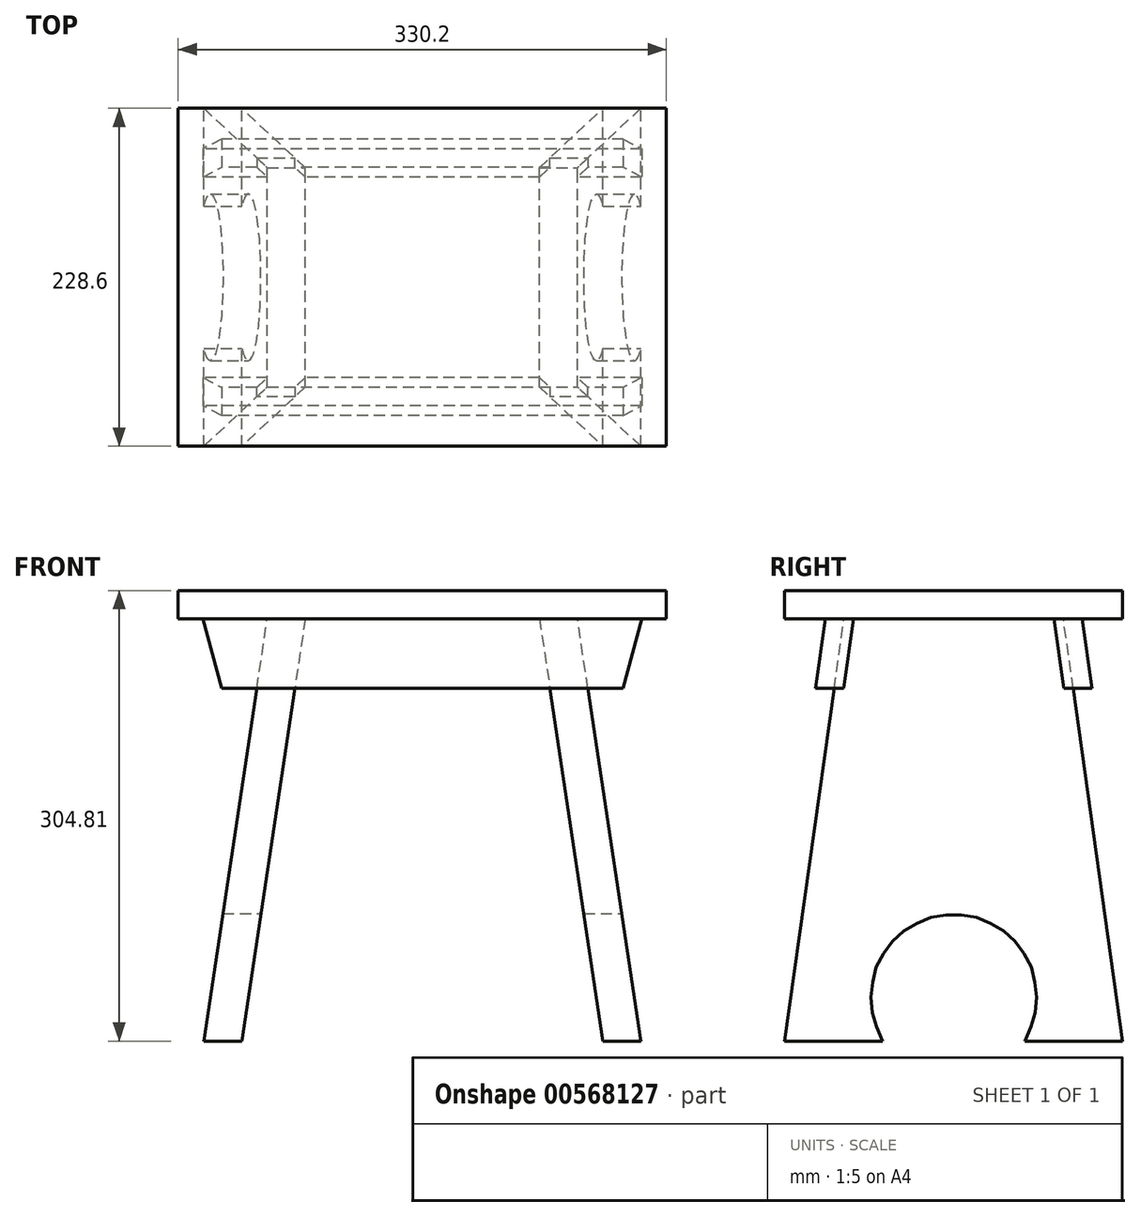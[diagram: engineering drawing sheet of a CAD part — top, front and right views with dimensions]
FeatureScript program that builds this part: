
annotation { "Feature Type Name" : "Feature", "Feature Type Description" : "" }
export const myFeature = defineFeature(function(context is Context, id is Id, definition is map)
    precondition{}
    {
        {
            var Q0;
            Q0=qCreatedBy(makeId("Front.planeOp"),FACE);
            var sketch = newSketch(context, id + "F0", { "sketchPlane" : qUnion([Q0])});
            skLineSegment(sketch, "E0.bottom", {"start": v(-165.1, 9.53) * mm, "end": v(165.1, 9.53) * mm});
            skLineSegment(sketch, "E0.top", {"start": v(-165.1, -9.52) * mm, "end": v(165.1, -9.52) * mm});
            skLineSegment(sketch, "E0.left", {"start": v(-165.1, 9.53) * mm, "end": v(-165.1, -9.52) * mm});
            skLineSegment(sketch, "E0.right", {"start": v(165.1, 9.53) * mm, "end": v(165.1, -9.52) * mm});
            skPoint(sketch, "E0.middle", {"position": v(0, 0) * mm});
            skLineSegment(sketch, "E1.bottom", {"start": v(-165.1, -9.52) * mm, "end": v(165.1, -9.52) * mm, "construction": true});
            skLineSegment(sketch, "E1.top", {"start": v(-165.1, -295.28) * mm, "end": v(165.1, -295.28) * mm, "construction": true});
            skLineSegment(sketch, "E1.left", {"start": v(-165.1, -9.52) * mm, "end": v(-165.1, -295.28) * mm, "construction": true});
            skLineSegment(sketch, "E1.right", {"start": v(165.1, -9.52) * mm, "end": v(165.1, -295.27) * mm, "construction": true});
            skLineSegment(sketch, "E2", {"start": v(104.9, -9.52) * mm, "end": v(147.77, -295.28) * mm});
            skLineSegment(sketch, "E3", {"start": v(147.77, -295.27) * mm, "end": v(122.1, -295.27) * mm});
            skLineSegment(sketch, "E4", {"start": v(122.1, -295.27) * mm, "end": v(79.2, -9.52) * mm});
            skLineSegment(sketch, "E5", {"start": v(79.2, -9.52) * mm, "end": v(104.9, -9.52) * mm});
            skLineSegment(sketch, "E6", {"start": v(0, 0) * mm, "end": v(0, -295.28) * mm, "construction": true});
            skLineSegment(sketch, "E7.MirrorCS", {"start": v(-104.9, -9.52) * mm, "end": v(-147.77, -295.28) * mm});
            skLineSegment(sketch, "E8.MirrorCS", {"start": v(-79.2, -9.52) * mm, "end": v(-104.9, -9.52) * mm});
            skLineSegment(sketch, "E9.MirrorCS", {"start": v(-147.77, -295.28) * mm, "end": v(-122.1, -295.28) * mm});
            skLineSegment(sketch, "E10.MirrorCS", {"start": v(-122.1, -295.28) * mm, "end": v(-79.2, -9.52) * mm});
            skLineSegment(sketch, "E11.top", {"start": v(-165.1, -56.79) * mm, "end": v(165.1, -56.79) * mm});
            skLineSegment(sketch, "E11.left", {"start": v(-165.1, -9.52) * mm, "end": v(-165.1, -56.79) * mm});
            skLineSegment(sketch, "E11.right", {"start": v(165.1, -9.52) * mm, "end": v(165.1, -56.79) * mm});
            skLineSegment(sketch, "E12", {"start": v(148.48, -9.52) * mm, "end": v(135.79, -56.79) * mm});
            skLineSegment(sketch, "E13.MirrorCS", {"start": v(-148.48, -9.52) * mm, "end": v(-135.79, -56.79) * mm});
            skSolve(sketch);
        }
        {
            var Q0;
            Q0=qCreatedBy(makeId("Front.planeOp"),FACE);
            var sketch = newSketch(context, id + "F1", { "sketchPlane" : qUnion([Q0])});
            skSolve(sketch);
        }
        {
            var Q0;
            Q0 = qSketchRegion(id + "F1", true);
            var Q1;
            Q1=makeQuery(id+"F0.imprint","IMPRINT",FACE,{"disambiguationData":[TD([[makeQuery(id+"F0.imprint","IMPRINT",EDGE,{"derivedFrom":sQuery(id+"F0.wireOp",EDGE,"E0.bottom")}),-1.0]])]});
            extrude(context, id + "F2", {"entities" : qUnion([Q0, Q1]), "endBound" : BoundingType.SYMMETRIC, "depth" : 228.6 * mm, "offsetDistance" : 25.4 * mm});
        }
        {
            var Q0;
            {var subQ0=sQuery(id+"F0.wireOp",EDGE,"E9.MirrorCS");Q0=makeQuery(id+"F0.imprint","IMPRINT",FACE,{"disambiguationData":[TD([[makeQuery(id+"F0.imprint","IMPRINT",EDGE,{"derivedFrom":subQ0}),1.0]])]});}
            var Q1;
            {var subQ0=sQuery(id+"F0.wireOp",EDGE,"E0.top");var subQ1=sQuery(id+"F0.wireOp",EDGE,"E7.MirrorCS");var subQ2=makeQuery(id+"F0.imprint","INTERSECT",VERTEX,{"derivedFrom":[subQ1,subQ0]});Q1=makeQuery(id+"F0.imprint","IMPRINT",FACE,{"disambiguationData":[TD([[makeQuery(id+"F0.imprint","IMPRINT",EDGE,{"disambiguationData":[TD([[subQ2,-1.0]])],"derivedFrom":subQ1}),1.0]])]});}
            var Q2;
            {var subQ0=sQuery(id+"F0.wireOp",EDGE,"E0.top");var subQ1=sQuery(id+"F0.wireOp",EDGE,"E2");var subQ2=makeQuery(id+"F0.imprint","INTERSECT",VERTEX,{"derivedFrom":[subQ1,subQ0]});Q2=makeQuery(id+"F0.imprint","IMPRINT",FACE,{"disambiguationData":[TD([[makeQuery(id+"F0.imprint","IMPRINT",EDGE,{"disambiguationData":[TD([[subQ2,-1.0]])],"derivedFrom":subQ1}),-1.0]])]});}
            var Q3;
            {var subQ0=sQuery(id+"F0.wireOp",EDGE,"E3");Q3=makeQuery(id+"F0.imprint","IMPRINT",FACE,{"disambiguationData":[TD([[makeQuery(id+"F0.imprint","IMPRINT",EDGE,{"derivedFrom":subQ0}),-1.0]])]});}
            var Q4;
            Q4=makeQuery(id+"F2.opExtrude","CAP_VERTEX",VERTEX,{"disambiguationData":[OSD([sQuery(id+"F0.wireOp",EDGE,"E0.right"),sQuery(id+"F0.wireOp",EDGE,"E0.top"),sQuery(id+"F0.wireOp",EDGE,"E11.right")])],"isStart":false});
            var Q5;
            Q5=makeQuery(id+"F2.opExtrude","CAP_VERTEX",VERTEX,{"disambiguationData":[OSD([sQuery(id+"F0.wireOp",EDGE,"E0.right"),sQuery(id+"F0.wireOp",EDGE,"E0.top"),sQuery(id+"F0.wireOp",EDGE,"E11.right")])],"isStart":true});
            extrude(context, id + "F3", {"entities" : qUnion([Q0, Q1, Q2, Q3]), "endBound" : BoundingType.UP_TO_VERTEX, "depth" : 25.4 * mm, "endBoundEntityVertex" : qUnion([Q4]), "offsetDistance" : 25.4 * mm, "hasSecondDirection" : true, "secondDirectionBound" : SecondDirectionBoundingType.UP_TO_VERTEX, "secondDirectionOppositeDirection" : true, "secondDirectionDepth" : 25.4 * mm, "secondDirectionBoundEntityVertex" : qUnion([Q5])});
        }
        {
            var Q0;
            Q0=qCreatedBy(makeId("Right.planeOp"),FACE);
            var sketch = newSketch(context, id + "F4", { "sketchPlane" : qUnion([Q0])});
            skLineSegment(sketch, "E14.0.0", {"start": v(114.3, -9.52) * mm, "end": v(-114.3, -9.52) * mm});
            skLineSegment(sketch, "E14.0.1", {"start": v(-114.3, -9.52) * mm, "end": v(-114.3, -295.28) * mm});
            skLineSegment(sketch, "E14.0.2", {"start": v(-114.3, -295.28) * mm, "end": v(114.3, -295.28) * mm});
            skLineSegment(sketch, "E14.0.3", {"start": v(114.3, -295.28) * mm, "end": v(114.3, -9.52) * mm});
            skLineSegment(sketch, "E15", {"start": v(-114.3, -295.27) * mm, "end": v(-74.14, -9.52) * mm});
            skLineSegment(sketch, "E16.MirrorCS", {"start": v(114.3, -295.27) * mm, "end": v(74.14, -9.52) * mm});
            skArc(sketch, "E17", {"start": v(48.03, -295.28) * mm, "mid": v(0, -209.18) * mm, "end": v(-48.03, -295.28) * mm});
            skLineSegment(sketch, "E18", {"start": v(0, -265.62) * mm, "end": v(0, -265.62) * mm});
            skSolve(sketch);
        }
        {
            var Q0;
            {var subQ0=sQuery(id+"F4.wireOp",EDGE,"E14.0.1");Q0=makeQuery(id+"F4.imprint","IMPRINT",FACE,{"disambiguationData":[TD([[makeQuery(id+"F4.imprint","IMPRINT",EDGE,{"derivedFrom":subQ0}),1.0]])]});}
            var Q1;
            {var subQ0=sQuery(id+"F4.wireOp",EDGE,"E17");Q1=makeQuery(id+"F4.imprint","IMPRINT",FACE,{"disambiguationData":[TD([[makeQuery(id+"F4.imprint","IMPRINT",EDGE,{"derivedFrom":subQ0}),1.0]])]});}
            var Q2;
            {var subQ0=sQuery(id+"F4.wireOp",EDGE,"E14.0.3");Q2=makeQuery(id+"F4.imprint","IMPRINT",FACE,{"disambiguationData":[TD([[makeQuery(id+"F4.imprint","IMPRINT",EDGE,{"derivedFrom":subQ0}),1.0]])]});}
            extrude(context, id + "F5", {"entities" : qUnion([Q0, Q1, Q2]), "operationType" : NewBodyOperationType.REMOVE, "endBound" : BoundingType.THROUGH_ALL, "oppositeDirection" : true, "depth" : 25.4 * mm, "offsetDistance" : 25.4 * mm, "hasSecondDirection" : true, "secondDirectionBound" : SecondDirectionBoundingType.THROUGH_ALL, "secondDirectionOppositeDirection" : false, "secondDirectionDepth" : 25.4 * mm});
        }
        {
            var Q0;
            Q0=qCreatedBy(makeId("Right.planeOp"),FACE);
            var sketch = newSketch(context, id + "F6", { "sketchPlane" : qUnion([Q0])});
            skLineSegment(sketch, "E19.0", {"start": v(-74.14, -9.52) * mm, "end": v(-114.3, -295.28) * mm});
            skLineSegment(sketch, "E20.0", {"start": v(-114.3, -9.52) * mm, "end": v(114.3, -9.52) * mm});
            skLineSegment(sketch, "E21.0", {"start": v(74.14, -9.53) * mm, "end": v(114.3, -295.28) * mm});
            skLineSegment(sketch, "E22", {"start": v(-86.97, -9.52) * mm, "end": v(-93.6, -56.79) * mm});
            skLineSegment(sketch, "E23", {"start": v(-93.6, -56.79) * mm, "end": v(-74.37, -56.79) * mm});
            skLineSegment(sketch, "E24", {"start": v(-74.37, -56.79) * mm, "end": v(-67.73, -9.52) * mm});
            skLineSegment(sketch, "E25", {"start": v(-67.73, -9.52) * mm, "end": v(-86.97, -9.52) * mm});
            skLineSegment(sketch, "E26", {"start": v(-74.37, -56.79) * mm, "end": v(14.93, -56.79) * mm, "construction": true});
            skLineSegment(sketch, "E27.MirrorCS", {"start": v(74.37, -56.79) * mm, "end": v(67.73, -9.52) * mm});
            skLineSegment(sketch, "E28.MirrorCS", {"start": v(67.73, -9.52) * mm, "end": v(86.97, -9.52) * mm});
            skLineSegment(sketch, "E29.MirrorCS", {"start": v(93.6, -56.79) * mm, "end": v(74.37, -56.79) * mm});
            skLineSegment(sketch, "E30.MirrorCS", {"start": v(86.97, -9.52) * mm, "end": v(93.6, -56.79) * mm});
            skSolve(sketch);
        }
        {
            var Q0;
            {var subQ5=sQuery(id+"F6.wireOp",EDGE,"E24");Q0=makeQuery(id+"F6.imprint","IMPRINT",FACE,{"disambiguationData":[TD([[makeQuery(id+"F6.imprint","IMPRINT",EDGE,{"derivedFrom":subQ5}),1.0]])]});}
            var Q1;
            {var subQ5=sQuery(id+"F6.wireOp",EDGE,"E22");Q1=makeQuery(id+"F6.imprint","IMPRINT",FACE,{"disambiguationData":[TD([[makeQuery(id+"F6.imprint","IMPRINT",EDGE,{"derivedFrom":subQ5}),1.0]])]});}
            var Q2;
            {var subQ5=sQuery(id+"F6.wireOp",EDGE,"E27.MirrorCS");Q2=makeQuery(id+"F6.imprint","IMPRINT",FACE,{"disambiguationData":[TD([[makeQuery(id+"F6.imprint","IMPRINT",EDGE,{"derivedFrom":subQ5}),-1.0]])]});}
            var Q3;
            {var subQ5=sQuery(id+"F6.wireOp",EDGE,"E30.MirrorCS");Q3=makeQuery(id+"F6.imprint","IMPRINT",FACE,{"disambiguationData":[TD([[makeQuery(id+"F6.imprint","IMPRINT",EDGE,{"derivedFrom":subQ5}),-1.0]])]});}
            var Q4;
            Q4=makeQuery(id+"F2.opExtrude","SWEPT_FACE",FACE,{"disambiguationData":[OSD([sQuery(id+"F0.wireOp",EDGE,"E0.right")])]});
            var Q5;
            Q5=makeQuery(id+"F2.opExtrude","SWEPT_FACE",FACE,{"disambiguationData":[OSD([sQuery(id+"F0.wireOp",EDGE,"E0.left")])]});
            extrude(context, id + "F7", {"entities" : qUnion([Q0, Q1, Q2, Q3]), "endBound" : BoundingType.UP_TO_SURFACE, "depth" : 25.4 * mm, "endBoundEntityFace" : qUnion([Q4]), "offsetDistance" : 25.4 * mm, "hasSecondDirection" : true, "secondDirectionBound" : SecondDirectionBoundingType.UP_TO_SURFACE, "secondDirectionOppositeDirection" : true, "secondDirectionDepth" : 25.4 * mm, "secondDirectionBoundEntityFace" : qUnion([Q5])});
        }
        {
            var Q0;
            {var subQ0=sQuery(id+"F0.wireOp",EDGE,"E11.left");Q0=makeQuery(id+"F0.imprint","IMPRINT",FACE,{"disambiguationData":[TD([[makeQuery(id+"F0.imprint","IMPRINT",EDGE,{"derivedFrom":subQ0}),1.0]])]});}
            var Q1;
            {var subQ0=sQuery(id+"F0.wireOp",EDGE,"E11.right");Q1=makeQuery(id+"F0.imprint","IMPRINT",FACE,{"disambiguationData":[TD([[makeQuery(id+"F0.imprint","IMPRINT",EDGE,{"derivedFrom":subQ0}),-1.0]])]});}
            extrude(context, id + "F8", {"entities" : qUnion([Q0, Q1]), "operationType" : NewBodyOperationType.REMOVE, "endBound" : BoundingType.THROUGH_ALL, "oppositeDirection" : true, "depth" : 25.4 * mm, "offsetDistance" : 25.4 * mm, "hasSecondDirection" : true, "secondDirectionBound" : SecondDirectionBoundingType.THROUGH_ALL, "secondDirectionOppositeDirection" : false, "secondDirectionDepth" : 25.4 * mm});
        }
        {
            var Q0;
            Q0=makeQuery(id+"F3.opExtrude","SWEPT_BODY",BODY,{"disambiguationData":[OSD([sQuery(id+"F0.wireOp",EDGE,"E7.MirrorCS"),sQuery(id+"F0.wireOp",EDGE,"E9.MirrorCS"),sQuery(id+"F0.wireOp",EDGE,"E10.MirrorCS"),sQuery(id+"F0.wireOp",EDGE,"E0.top")])]});
            var Q1;
            Q1=makeQuery(id+"F7.opExtrude","SWEPT_BODY",BODY,{"disambiguationData":[OSD([sQuery(id+"F6.wireOp",EDGE,"E27.MirrorCS"),sQuery(id+"F6.wireOp",EDGE,"E28.MirrorCS"),sQuery(id+"F6.wireOp",EDGE,"E29.MirrorCS"),sQuery(id+"F6.wireOp",EDGE,"E30.MirrorCS")])]});
            booleanBodies(context, id + "F9", {"operationType" : BooleanOperationType.SUBTRACTION, "tools" : qUnion([Q0]), "targets" : qUnion([Q1]), "keepTools" : true});
        }
        {
            var Q0;
            Q0=makeQuery(id+"F3.opExtrude","SWEPT_BODY",BODY,{"disambiguationData":[OSD([sQuery(id+"F0.wireOp",EDGE,"E2"),sQuery(id+"F0.wireOp",EDGE,"E3"),sQuery(id+"F0.wireOp",EDGE,"E4"),sQuery(id+"F0.wireOp",EDGE,"E0.top")])]});
            var Q1;
            Q1=makeQuery(id+"F7.opExtrude","SWEPT_BODY",BODY,{"disambiguationData":[OSD([sQuery(id+"F6.wireOp",EDGE,"E27.MirrorCS"),sQuery(id+"F6.wireOp",EDGE,"E28.MirrorCS"),sQuery(id+"F6.wireOp",EDGE,"E29.MirrorCS"),sQuery(id+"F6.wireOp",EDGE,"E30.MirrorCS")])]});
            booleanBodies(context, id + "F10", {"operationType" : BooleanOperationType.SUBTRACTION, "tools" : qUnion([Q0]), "targets" : qUnion([Q1]), "keepTools" : true});
        }
        {
            var Q0;
            Q0=makeQuery(id+"F3.opExtrude","SWEPT_BODY",BODY,{"disambiguationData":[OSD([sQuery(id+"F0.wireOp",EDGE,"E2"),sQuery(id+"F0.wireOp",EDGE,"E3"),sQuery(id+"F0.wireOp",EDGE,"E4"),sQuery(id+"F0.wireOp",EDGE,"E0.top")])]});
            var Q1;
            Q1=makeQuery(id+"F7.opExtrude","SWEPT_BODY",BODY,{"disambiguationData":[OSD([sQuery(id+"F6.wireOp",EDGE,"E22"),sQuery(id+"F6.wireOp",EDGE,"E23"),sQuery(id+"F6.wireOp",EDGE,"E24"),sQuery(id+"F6.wireOp",EDGE,"E25")])]});
            booleanBodies(context, id + "F11", {"operationType" : BooleanOperationType.SUBTRACTION, "tools" : qUnion([Q0]), "targets" : qUnion([Q1]), "keepTools" : true});
        }
        {
            var Q0;
            Q0=makeQuery(id+"F3.opExtrude","SWEPT_BODY",BODY,{"disambiguationData":[OSD([sQuery(id+"F0.wireOp",EDGE,"E7.MirrorCS"),sQuery(id+"F0.wireOp",EDGE,"E9.MirrorCS"),sQuery(id+"F0.wireOp",EDGE,"E10.MirrorCS"),sQuery(id+"F0.wireOp",EDGE,"E0.top")])]});
            var Q1;
            Q1=makeQuery(id+"F7.opExtrude","SWEPT_BODY",BODY,{"disambiguationData":[OSD([sQuery(id+"F6.wireOp",EDGE,"E22"),sQuery(id+"F6.wireOp",EDGE,"E23"),sQuery(id+"F6.wireOp",EDGE,"E24"),sQuery(id+"F6.wireOp",EDGE,"E25")])]});
            booleanBodies(context, id + "F12", {"operationType" : BooleanOperationType.SUBTRACTION, "tools" : qUnion([Q0]), "targets" : qUnion([Q1]), "keepTools" : true});
        }
    });
